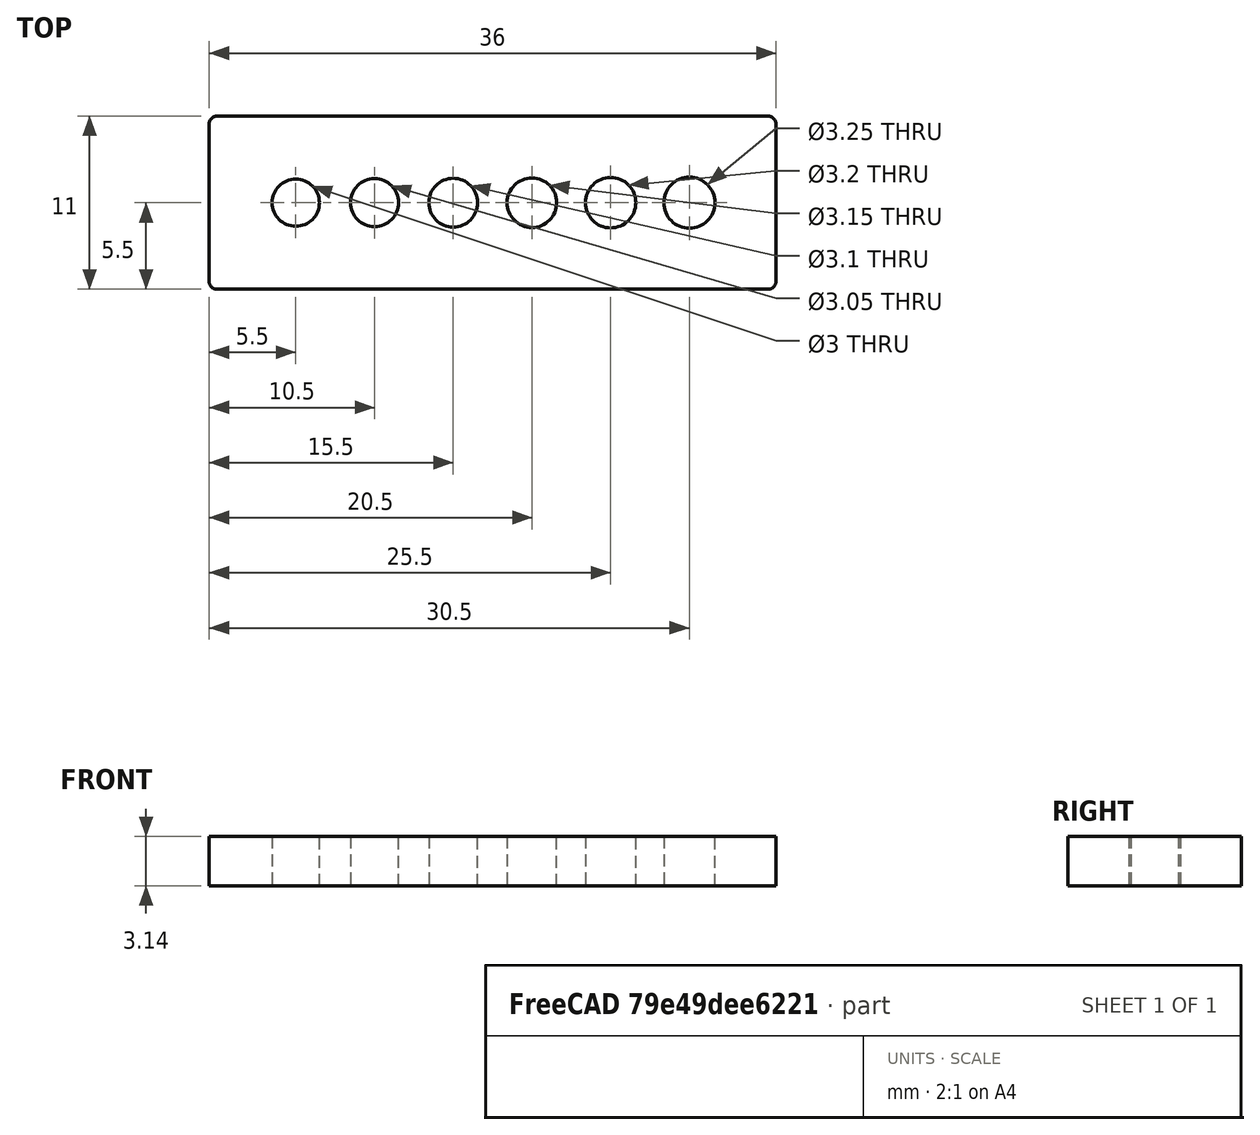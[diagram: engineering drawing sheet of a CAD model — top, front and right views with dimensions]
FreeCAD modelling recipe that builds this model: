
FCSTD DOCUMENT  (FreeCAD 1.0R39285 (Git))
Label: Hole-Tests
License: Creative Commons Attribution 4.0
objects: Sketcher::SketchObject×1, PartDesign::Pad×1, PartDesign::Body×1
note: 6 computed .brp shape members not serialized (recipe doc carries the construction recipe); baked Part::Feature solids carry a one-line shape summary decoded from their .brp

FEATURE [Sketcher::SketchObject] Sketch
  ArcFitTolerance = 1e-06
  AttachmentSupport = -> [XY_Plane]
  FullyConstrained = true
  MakeInternals = false
  MapMode = 5
  sketch-geometry (91):
    g0: LineSegment StartX=-20 StartY=5 StartZ=0 EndX=-20 EndY=-5 EndZ=0
    g1: LineSegment StartX=-19.5 StartY=-5.5 StartZ=0 EndX=19.5 EndY=-5.5 EndZ=0
    g2: LineSegment StartX=20 StartY=-5 StartZ=0 EndX=20 EndY=5 EndZ=0
    g3: LineSegment StartX=19.5 StartY=5.5 StartZ=0 EndX=-19.5 EndY=5.5 EndZ=0
    g4: ArcOfCircle CenterX=-19.5 CenterY=5 CenterZ=0 NormalX=0 NormalY=0 NormalZ=1 AngleXU=0 Radius=0.5 StartAngle=1.5708 EndAngle=3.14159
    g5: ArcOfCircle CenterX=-19.5 CenterY=-5 CenterZ=0 NormalX=0 NormalY=0 NormalZ=1 AngleXU=0 Radius=0.5 StartAngle=3.14159 EndAngle=4.71239
    g6: ArcOfCircle CenterX=19.5 CenterY=-5 CenterZ=0 NormalX=0 NormalY=0 NormalZ=1 AngleXU=0 Radius=0.5 StartAngle=4.71239 EndAngle=6.28319
    g7: ArcOfCircle CenterX=19.5 CenterY=5 CenterZ=0 NormalX=0 NormalY=0 NormalZ=1 AngleXU=0 Radius=0.5 StartAngle=0 EndAngle=1.5708
    g8: GeomPoint [constr] X=-20 Y=5.5 Z=0
    g9: GeomPoint [constr] X=20 Y=-5.5 Z=0
    g10: ArcOfCircle CenterX=-14.5 CenterY=0 CenterZ=0 NormalX=0 NormalY=0 NormalZ=1 AngleXU=0 Radius=1.45 StartAngle=1.5708 EndAngle=7.84035
    g11: Circle CenterX=-7.5 CenterY=0 CenterZ=0 NormalX=0 NormalY=0 NormalZ=1 AngleXU=0 Radius=1.45
    g12: Circle CenterX=-2.5 CenterY=0 CenterZ=0 NormalX=0 NormalY=0 NormalZ=1 AngleXU=0 Radius=1.45
    g13: Circle CenterX=2.5 CenterY=0 CenterZ=0 NormalX=0 NormalY=0 NormalZ=1 AngleXU=0 Radius=1.4
    g14: Circle CenterX=7.5 CenterY=0 CenterZ=0 NormalX=0 NormalY=0 NormalZ=1 AngleXU=0 Radius=1.45
    g15: Circle CenterX=12.5 CenterY=0 CenterZ=0 NormalX=0 NormalY=0 NormalZ=1 AngleXU=0 Radius=1.5
    g16: LineSegment StartX=7.5 StartY=1.45 StartZ=0 EndX=8.79904 EndY=2.2 EndZ=0
    g17: LineSegment [constr] StartX=7.5 StartY=1.45 StartZ=0 EndX=7.5 EndY=-1.45 EndZ=0
    g18: LineSegment [constr] StartX=8.95 StartY=0 StartZ=0 EndX=6.05 EndY=0 EndZ=0
    g19: LineSegment [constr] StartX=6.4747 StartY=1.0253 StartZ=0 EndX=8.5253 EndY=-1.0253 EndZ=0
    g20: LineSegment [constr] StartX=6.4747 StartY=-1.0253 StartZ=0 EndX=8.5253 EndY=1.0253 EndZ=0
    g21: GeomPoint [constr] X=7.5 Y=0 Z=0
    g22: LineSegment StartX=8.5253 StartY=1.0253 StartZ=0 EndX=9.97419 EndY=0.637076 EndZ=0
    g23: LineSegment StartX=8.95 StartY=0 StartZ=0 EndX=9.7 EndY=-1.29904 EndZ=0
    g24: LineSegment StartX=8.5253 StartY=-1.0253 StartZ=0 EndX=8.13708 EndY=-2.47419 EndZ=0
    g25: LineSegment StartX=7.5 StartY=-1.45 StartZ=0 EndX=6.20096 EndY=-2.2 EndZ=0
    g26: LineSegment StartX=6.4747 StartY=-1.0253 StartZ=0 EndX=5.02581 EndY=-0.637076 EndZ=0
    g27: LineSegment StartX=6.05 StartY=0 StartZ=0 EndX=5.3 EndY=1.29904 EndZ=0
    g28: LineSegment StartX=6.4747 StartY=1.0253 StartZ=0 EndX=6.86292 EndY=2.47419 EndZ=0
    g29: LineSegment [constr] StartX=2.5 StartY=1.4 StartZ=0 EndX=2.5 EndY=-1.4 EndZ=0
    g30: LineSegment [constr] StartX=1.1 StartY=0 StartZ=0 EndX=3.9 EndY=0 EndZ=0
    g31: LineSegment [constr] StartX=1.51005 StartY=0.989949 StartZ=0 EndX=3.48995 EndY=-0.989949 EndZ=0
    g32: LineSegment [constr] StartX=1.51005 StartY=-0.989949 StartZ=0 EndX=3.48995 EndY=0.989949 EndZ=0
    g33: LineSegment StartX=2.5 StartY=1.4 StartZ=0 EndX=3.79904 EndY=2.15 EndZ=0
    g34: LineSegment StartX=3.48995 StartY=0.989949 StartZ=0 EndX=4.93884 EndY=0.601721 EndZ=0
    g35: LineSegment StartX=3.9 StartY=0 StartZ=0 EndX=4.65 EndY=-1.29904 EndZ=0
    g36: LineSegment StartX=3.48995 StartY=-0.989949 StartZ=0 EndX=3.10172 EndY=-2.43884 EndZ=0
    g37: LineSegment StartX=2.5 StartY=-1.4 StartZ=0 EndX=1.20096 EndY=-2.15 EndZ=0
    g38: LineSegment StartX=1.51005 StartY=-0.989949 StartZ=0 EndX=0.0611618 EndY=-0.601721 EndZ=0
    g39: LineSegment StartX=1.1 StartY=0 StartZ=0 EndX=0.35 EndY=1.29904 EndZ=0
    g40: LineSegment StartX=1.51005 StartY=0.989949 StartZ=0 EndX=1.89828 EndY=2.43884 EndZ=0
    g41: LineSegment [constr] StartX=12.5 StartY=1.5 StartZ=0 EndX=12.5 EndY=-1.5 EndZ=0
    g42: LineSegment [constr] StartX=14 StartY=0 StartZ=0 EndX=11 EndY=0 EndZ=0
    g43: LineSegment [constr] StartX=13.5607 StartY=-1.06066 StartZ=0 EndX=11.4393 EndY=1.06066 EndZ=0
    g44: LineSegment [constr] StartX=13.5607 StartY=1.06066 StartZ=0 EndX=11.4393 EndY=-1.06066 EndZ=0
    g45: LineSegment StartX=12.5 StartY=1.5 StartZ=0 EndX=13.799 EndY=2.25 EndZ=0
    g46: LineSegment StartX=13.5607 StartY=1.06066 StartZ=0 EndX=15.0095 EndY=0.672432 EndZ=0
    g47: LineSegment StartX=14 StartY=0 StartZ=0 EndX=14.75 EndY=-1.29904 EndZ=0
    g48: LineSegment StartX=13.5607 StartY=-1.06066 StartZ=0 EndX=13.1724 EndY=-2.50955 EndZ=0
    g49: LineSegment StartX=12.5 StartY=-1.5 StartZ=0 EndX=11.201 EndY=-2.25 EndZ=0
    g50: LineSegment StartX=11.4393 StartY=-1.06066 StartZ=0 EndX=9.99045 EndY=-0.672432 EndZ=0
    g51: LineSegment StartX=11 StartY=0 StartZ=0 EndX=10.25 EndY=1.29904 EndZ=0
    g52: LineSegment StartX=11.4393 StartY=1.06066 StartZ=0 EndX=11.8276 EndY=2.50955 EndZ=0
    g53: LineSegment [constr] StartX=-14.5 StartY=1.45 StartZ=0 EndX=-14.5 EndY=-1.45 EndZ=0
    g54: LineSegment [constr] StartX=-15.95 StartY=0 StartZ=0 EndX=-13.05 EndY=0 EndZ=0
    g55: LineSegment [constr] StartX=-13.4747 StartY=1.0253 StartZ=0 EndX=-15.5253 EndY=-1.0253 EndZ=0
    g56: LineSegment [constr] StartX=-15.5253 StartY=1.0253 StartZ=0 EndX=-13.4747 EndY=-1.0253 EndZ=0
    g57: LineSegment [constr] StartX=-7.5 StartY=1.45 StartZ=0 EndX=-7.5 EndY=-1.45 EndZ=0
    g58: LineSegment [constr] StartX=-6.05 StartY=0 StartZ=0 EndX=-8.95 EndY=0 EndZ=0
    g59: LineSegment [constr] StartX=-8.5253 StartY=-1.0253 StartZ=0 EndX=-6.4747 EndY=1.0253 EndZ=0
    g60: LineSegment [constr] StartX=-8.5253 StartY=1.0253 StartZ=0 EndX=-6.4747 EndY=-1.0253 EndZ=0
    g61: LineSegment [constr] StartX=-2.5 StartY=1.45 StartZ=0 EndX=-2.5 EndY=-1.45 EndZ=0
    g62: LineSegment [constr] StartX=-3.95 StartY=0 StartZ=0 EndX=-1.05 EndY=0 EndZ=0
    g63: LineSegment [constr] StartX=-1.4747 StartY=1.0253 StartZ=0 EndX=-3.5253 EndY=-1.0253 EndZ=0
    g64: LineSegment [constr] StartX=-3.5253 StartY=1.0253 StartZ=0 EndX=-1.4747 EndY=-1.0253 EndZ=0
    g65: LineSegment StartX=-14.5 StartY=1.45 StartZ=0 EndX=-12.3349 EndY=2.7 EndZ=0
    g66: LineSegment StartX=-13.4747 StartY=1.0253 StartZ=0 EndX=-11.0599 EndY=0.378257 EndZ=0
    g67: LineSegment StartX=-13.05 StartY=0 StartZ=0 EndX=-11.8 EndY=-2.16506 EndZ=0
    g68: LineSegment StartX=-13.4747 StartY=-1.0253 StartZ=0 EndX=-14.1217 EndY=-3.44012 EndZ=0
    g69: LineSegment StartX=-14.5 StartY=-1.45 StartZ=0 EndX=-16.6651 EndY=-2.7 EndZ=0
    g70: LineSegment StartX=-15.5253 StartY=-1.0253 StartZ=0 EndX=-17.9401 EndY=-0.378257 EndZ=0
    g71: LineSegment StartX=-15.95 StartY=0 StartZ=0 EndX=-17.2 EndY=2.16506 EndZ=0
    g72: LineSegment StartX=-15.5253 StartY=1.0253 StartZ=0 EndX=-14.8783 EndY=3.44012 EndZ=0
    g73: LineSegment StartX=-7.5 StartY=1.45 StartZ=0 EndX=-6.35093 EndY=2.41418 EndZ=0
    g74: LineSegment StartX=-6.4747 StartY=1.0253 StartZ=0 EndX=-4.9804 EndY=0.894571 EndZ=0
    g75: LineSegment StartX=-6.05 StartY=0 StartZ=0 EndX=-5.08582 EndY=-1.14907 EndZ=0
    g76: LineSegment StartX=-6.4747 StartY=-1.0253 StartZ=0 EndX=-6.60543 EndY=-2.5196 EndZ=0
    g77: LineSegment StartX=-7.5 StartY=-1.45 StartZ=0 EndX=-8.64907 EndY=-2.41418 EndZ=0
    g78: LineSegment StartX=-8.5253 StartY=-1.0253 StartZ=0 EndX=-10.0196 EndY=-0.894571 EndZ=0
    g79: LineSegment StartX=-8.95 StartY=0 StartZ=0 EndX=-9.91418 EndY=1.14907 EndZ=0
    g80: LineSegment StartX=-8.5253 StartY=1.0253 StartZ=0 EndX=-8.39457 EndY=2.5196 EndZ=0
    g81: LineSegment StartX=-2.5 StartY=1.45 StartZ=0 EndX=-1.09046 EndY=1.96303 EndZ=0
    g82: LineSegment StartX=-1.4747 StartY=1.0253 StartZ=0 EndX=-0.115233 EndY=0.391377 EndZ=0
    g83: LineSegment StartX=-1.05 StartY=0 StartZ=0 EndX=-0.53697 EndY=-1.40954 EndZ=0
    g84: LineSegment StartX=-1.4747 StartY=-1.0253 StartZ=0 EndX=-2.10862 EndY=-2.38477 EndZ=0
    g85: LineSegment StartX=-2.5 StartY=-1.45 StartZ=0 EndX=-3.90954 EndY=-1.96303 EndZ=0
    g86: LineSegment StartX=-3.5253 StartY=-1.0253 StartZ=0 EndX=-4.88477 EndY=-0.391377 EndZ=0
    g87: LineSegment StartX=-3.95 StartY=0 StartZ=0 EndX=-4.46303 EndY=1.40954 EndZ=0
    g88: LineSegment StartX=-3.5253 StartY=1.0253 StartZ=0 EndX=-2.89138 EndY=2.38477 EndZ=0
    g89: LineSegment StartX=-12.3349 StartY=2.7 StartZ=0 EndX=-12.3299 EndY=2.69134 EndZ=0
    g90: LineSegment StartX=-12.3299 StartY=2.69134 StartZ=0 EndX=-14.4802 EndY=1.44987 EndZ=0
  constraints (285):
    c: Tangent(g0,g4) = -1.5708
    c: Tangent(g0,g5) = -1.5708
    c: Tangent(g1,g5) = -1.5708
    c: Tangent(g1,g6) = -1.5708
    c: Tangent(g2,g6) = -1.5708
    c: Tangent(g2,g7) = -1.5708
    c: Tangent(g3,g7) = -1.5708
    c: Tangent(g3,g4) = -1.5708
    c: Vertical(g0)
    c: Vertical(g2)
    c: Horizontal(g1)
    c: Horizontal(g3)
    c: Equal(g5,g6)
    c: PointOnObject(g8,g0)
    c: PointOnObject(g8,g3)
    c: PointOnObject(g9,g1)
    c: PointOnObject(g9,g2)
    c: Symmetric(g4,g7,g-2)
    c: Symmetric(g4,g5,g-1)
    c: PointOnObject(g15,g-1)
    c: PointOnObject(g14,g-1)
    c: PointOnObject(g13,g-1)
    c: PointOnObject(g11,g-1)
    c: PointOnObject(g10,g-1)
    c: Diameter(g10) = 2.9
    c: Diameter(g11) = 2.9
    c: Diameter(g12) = 2.9
    c: Diameter(g13) = 2.8
    c: Diameter(g14) = 2.9
    c: Diameter(g15) = 3
    c: DistanceX(g10,g11) = 7
    c: DistanceX(g11,g12) = 5
    c: DistanceX(g12,g13) = 5
    c: DistanceX(g13,g14) = 5
    c: DistanceX(g14,g15) = 5
    c: Symmetric(g12,g13,g-2)
    c: Diameter(g4) = 1
    c: DistanceX(g15,g7) = 7
    c: DistanceY(g15,g7) = 5
    c: PointOnObject(g16,g14)
    c: Coincident(g17,g16)
    c: PointOnObject(g17,g14)
    c: Vertical(g17)
    c: PointOnObject(g18,g14)
    c: PointOnObject(g19,g14)
    c: PointOnObject(g19,g14)
    c: PointOnObject(g20,g14)
    c: PointOnObject(g20,g14)
    c: Angle(g17,g19) = 0.785398
    c: Angle(g18,g20) = 0.785398
    c: Symmetric(g18,g18,g21)
    c: PointOnObject(g21,g19)
    c: PointOnObject(g21,g20)
    c: PointOnObject(g21,g17)
    c: Coincident(g21,g14)
    c: Angle(g17,g16) = 2.0944
    c: Distance(g16) = 1.5
    c: Coincident(g22,g20)
    c: Coincident(g23,g18)
    c: Coincident(g24,g19)
    c: Coincident(g25,g17)
    c: Coincident(g26,g20)
    c: Coincident(g27,g18)
    c: Coincident(g28,g19)
    c: Equal(g16,g28)
    c: Equal(g28,g27)
    c: Equal(g27,g26)
    c: Equal(g26,g25)
    c: Equal(g25,g24)
    c: Equal(g24,g23)
    c: Equal(g23,g22)
    c: Angle(g20,g22) = 2.0944
    c: Angle(g18,g23) = 2.0944
    c: Horizontal(g18)
    c: Angle(g19,g24) = 2.0944
    c: Angle(g17,g25) = 2.0944
    c: Angle(g20,g26) = 2.0944
    c: Angle(g18,g27) = 2.0944
    c: Angle(g19,g28) = 2.0944
    c: PointOnObject(g29,g13)
    c: PointOnObject(g29,g13)
    c: Vertical(g29)
    c: PointOnObject(g30,g13)
    c: PointOnObject(g30,g13)
    c: PointOnObject(g31,g13)
    c: PointOnObject(g31,g13)
    c: PointOnObject(g32,g13)
    c: PointOnObject(g32,g13)
    c: Angle(g30,g32) = 0.785398
    c: Horizontal(g30)
    c: Angle(g29,g31) = 0.785398
    c: PointOnObject(g13,g30)
    c: PointOnObject(g13,g31)
    c: PointOnObject(g13,g32)
    c: PointOnObject(g13,g29)
    c: Coincident(g33,g29)
    c: Coincident(g34,g32)
    c: Coincident(g35,g30)
    c: Coincident(g36,g31)
    c: Coincident(g37,g29)
    c: Coincident(g38,g32)
    c: Coincident(g39,g30)
    c: Coincident(g40,g31)
    c: Distance(g33) = 1.5
    c: Equal(g33,g40)
    c: Equal(g40,g39)
    c: Equal(g39,g38)
    c: Equal(g38,g37)
    c: Equal(g37,g36)
    c: Equal(g36,g35)
    c: Equal(g35,g34)
    c: Angle(g29,g33) = 2.0944
    c: Angle(g32,g34) = 2.0944
    c: Angle(g30,g35) = 2.0944
    c: Angle(g31,g36) = 2.0944
    c: Angle(g29,g37) = 2.0944
    c: Angle(g32,g38) = 2.0944
    c: Angle(g30,g39) = 2.0944
    c: Angle(g31,g40) = 2.0944
    c: PointOnObject(g41,g15)
    c: PointOnObject(g41,g15)
    c: PointOnObject(g42,g15)
    c: PointOnObject(g42,g15)
    c: PointOnObject(g43,g15)
    c: PointOnObject(g43,g15)
    c: PointOnObject(g44,g15)
    c: PointOnObject(g44,g15)
    c: Horizontal(g42)
    c: Vertical(g41)
    c: Angle(g43,g42) = 0.785398
    c: Angle(g42,g44) = 0.785398
    c: PointOnObject(g15,g44)
    c: PointOnObject(g15,g41)
    c: PointOnObject(g15,g42)
    c: PointOnObject(g15,g43)
    c: Coincident(g45,g41)
    c: Coincident(g46,g44)
    c: Coincident(g47,g42)
    c: Coincident(g48,g43)
    c: Coincident(g49,g41)
    c: Coincident(g50,g44)
    c: Coincident(g51,g42)
    c: Coincident(g52,g43)
    c: Distance(g45) = 1.5
    c: Equal(g45,g46)
    c: Equal(g46,g47)
    c: Equal(g47,g48)
    c: Equal(g48,g49)
    c: Equal(g49,g50)
    c: Equal(g50,g51)
    c: Equal(g51,g52)
    c: Angle(g41,g45) = 2.0944
    c: Angle(g44,g46) = 2.0944
    c: Angle(g42,g47) = 2.0944
    c: Angle(g43,g48) = 2.0944
    c: Angle(g41,g49) = 2.0944
    c: Angle(g44,g50) = 2.0944
    c: Angle(g42,g51) = 2.0944
    c: Angle(g43,g52) = 2.0944
    c: PointOnObject(g53,g10)
    c: Vertical(g53)
    c: PointOnObject(g54,g10)
    c: PointOnObject(g54,g10)
    c: PointOnObject(g55,g10)
    c: PointOnObject(g55,g10)
    c: PointOnObject(g56,g10)
    c: PointOnObject(g56,g10)
    c: Horizontal(g54)
    c: Angle(g56,g54) = 0.785398
    c: Angle(g54,g55) = 0.785398
    c: PointOnObject(g10,g55)
    c: PointOnObject(g10,g56)
    c: PointOnObject(g10,g54)
    c: PointOnObject(g10,g53)
    c: PointOnObject(g57,g11)
    c: PointOnObject(g57,g11)
    c: PointOnObject(g58,g11)
    c: PointOnObject(g58,g11)
    c: PointOnObject(g59,g11)
    c: PointOnObject(g59,g11)
    c: PointOnObject(g60,g11)
    c: PointOnObject(g60,g11)
    c: PointOnObject(g61,g12)
    c: PointOnObject(g61,g12)
    c: PointOnObject(g62,g12)
    c: PointOnObject(g62,g12)
    c: PointOnObject(g63,g12)
    c: PointOnObject(g63,g12)
    c: PointOnObject(g64,g12)
    c: PointOnObject(g64,g12)
    c: Horizontal(g62)
    c: Horizontal(g58)
    c: Vertical(g57)
    c: Vertical(g61)
    c: Angle(g63,g61) = 0.785398
    c: Angle(g64,g62) = 0.785398
    c: Angle(g60,g58) = 0.785398
    c: Angle(g59,g57) = 0.785398
    c: PointOnObject(g11,g59)
    c: PointOnObject(g11,g60)
    c: PointOnObject(g11,g57)
    c: PointOnObject(g11,g58)
    c: PointOnObject(g12,g64)
    c: PointOnObject(g12,g61)
    c: PointOnObject(g12,g63)
    c: PointOnObject(g12,g62)
    c: Coincident(g65,g53)
    c: Coincident(g66,g55)
    c: Coincident(g67,g54)
    c: Coincident(g68,g56)
    c: Coincident(g69,g53)
    c: Coincident(g70,g55)
    c: Coincident(g71,g54)
    c: Coincident(g72,g56)
    c: Distance(g65) = 2.5
    c: Equal(g65,g66)
    c: Equal(g66,g67)
    c: Equal(g67,g68)
    c: Equal(g68,g69)
    c: Equal(g69,g70)
    c: Equal(g70,g72)
    c: Equal(g72,g71)
    c: Angle(g53,g65) = 2.0944
    c: Angle(g55,g66) = 2.0944
    c: Angle(g54,g67) = 2.0944
    c: Angle(g56,g68) = 2.0944
    c: Angle(g53,g69) = 2.0944
    c: Angle(g55,g70) = 2.0944
    c: Angle(g54,g71) = 2.0944
    c: Angle(g56,g72) = 2.0944
    c: Coincident(g73,g57)
    c: Coincident(g74,g59)
    c: Coincident(g75,g58)
    c: Coincident(g76,g60)
    c: Coincident(g77,g57)
    c: Coincident(g78,g59)
    c: Coincident(g79,g58)
    c: Coincident(g80,g60)
    c: Coincident(g81,g61)
    c: Coincident(g82,g63)
    c: Coincident(g83,g62)
    c: Coincident(g84,g64)
    c: Coincident(g85,g61)
    c: Coincident(g86,g63)
    c: Coincident(g87,g62)
    c: Coincident(g88,g64)
    c: Distance(g73) = 1.5
    c: Distance(g81) = 1.5
    c: Equal(g81,g82)
    c: Equal(g82,g83)
    c: Equal(g83,g84)
    c: Equal(g84,g86)
    c: Equal(g86,g85)
    c: Equal(g85,g87)
    c: Equal(g87,g88)
    c: Angle(g61,g81) = 1.91986
    c: Angle(g63,g82) = 1.91986
    c: Angle(g62,g83) = 1.91986
    c: Angle(g64,g84) = 1.91986
    c: Angle(g61,g85) = 1.91986
    c: Angle(g63,g86) = 1.91986
    c: Angle(g62,g87) = 1.91986
    c: Angle(g64,g88) = 1.91986
    c: Angle(g57,g73) = 2.26893
    c: Angle(g59,g74) = 2.26893
    c: Angle(g58,g75) = 2.26893
    c: Angle(g60,g76) = 2.26893
    c: Angle(g57,g77) = 2.26893
    c: Angle(g59,g78) = 2.26893
    c: Angle(g58,g79) = 2.26893
    c: Angle(g60,g80) = 2.26893
    c: Equal(g73,g74)
    c: Equal(g74,g75)
    c: Equal(g75,g76)
    c: Equal(g76,g77)
    c: Equal(g77,g78)
    c: Equal(g78,g79)
    c: Equal(g79,g80)
    c: Coincident(g65,g89)
    c: Coincident(g89,g90)
    c: Distance(g89) = 0.01
    c: Parallel(g90,g65)
    c: Angle(g65,g89) = 1.5708
    c: Coincident(g10,g90)
    c: Coincident(g10,g65)
FEATURE [PartDesign::Pad] Pad
  Direction = (0,0,1)
  Length = 3.14
  Length2 = 10
  Profile = -> Sketch
  ReferenceAxis = -> Sketch [N_Axis]
  Refine = true
  Suppressed = false
  Type = 0
FEATURE [PartDesign::Body] Body
  AllowCompound = false
  Group = -> [Sketch,Pad]
  Origin = -> Origin
  Tip = -> Pad
